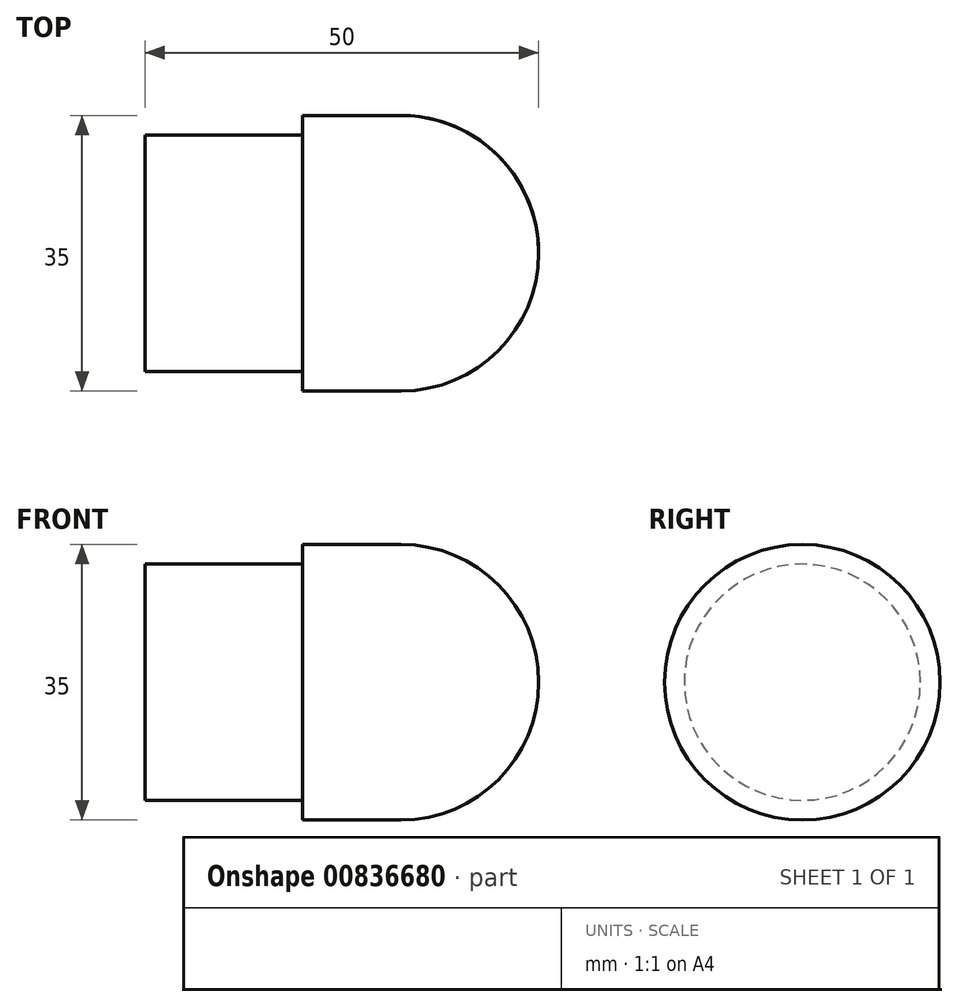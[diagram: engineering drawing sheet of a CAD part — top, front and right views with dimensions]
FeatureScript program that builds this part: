
annotation { "Feature Type Name" : "Feature", "Feature Type Description" : "" }
export const myFeature = defineFeature(function(context is Context, id is Id, definition is map)
    precondition{}
    {
        {
            var Q0;
            Q0=qCreatedBy(makeId("Top.planeOp"),FACE);
            var sketch = newSketch(context, id + "F0", { "sketchPlane" : qUnion([Q0])});
            skLineSegment(sketch, "E0", {"start": v(25, 0) * mm, "end": v(-25, 0) * mm});
            skLineSegment(sketch, "E1", {"start": v(-25, 0) * mm, "end": v(-25, 15) * mm});
            skLineSegment(sketch, "E2", {"start": v(-25, 15) * mm, "end": v(-5, 15) * mm});
            skLineSegment(sketch, "E3", {"start": v(-5, 15) * mm, "end": v(-5, 17.5) * mm});
            skLineSegment(sketch, "E4", {"start": v(-5, 17.5) * mm, "end": v(7.5, 17.5) * mm});
            skArc(sketch, "E5", {"start": v(25, 0) * mm, "mid": v(19.87, 12.37) * mm, "end": v(7.5, 17.5) * mm});
            skSolve(sketch);
        }
        {
            var Q0;
            Q0=makeQuery(id+"F0.imprint","IMPRINT",FACE,{"disambiguationData":[TD([[makeQuery(id+"F0.imprint","IMPRINT",EDGE,{"derivedFrom":sQuery(id+"F0.wireOp",EDGE,"E0")}),-1.0]])]});
            var Q1;
            Q1=sQuery(id+"F0.wireOp",EDGE,"E0");
            revolve(context, id + "F1", {"surfaceOperationType" : NewSurfaceOperationType.NEW, "entities" : qUnion([Q0]), "axis" : qUnion([Q1]), "revolveType" : RevolveType.FULL});
        }
    });
